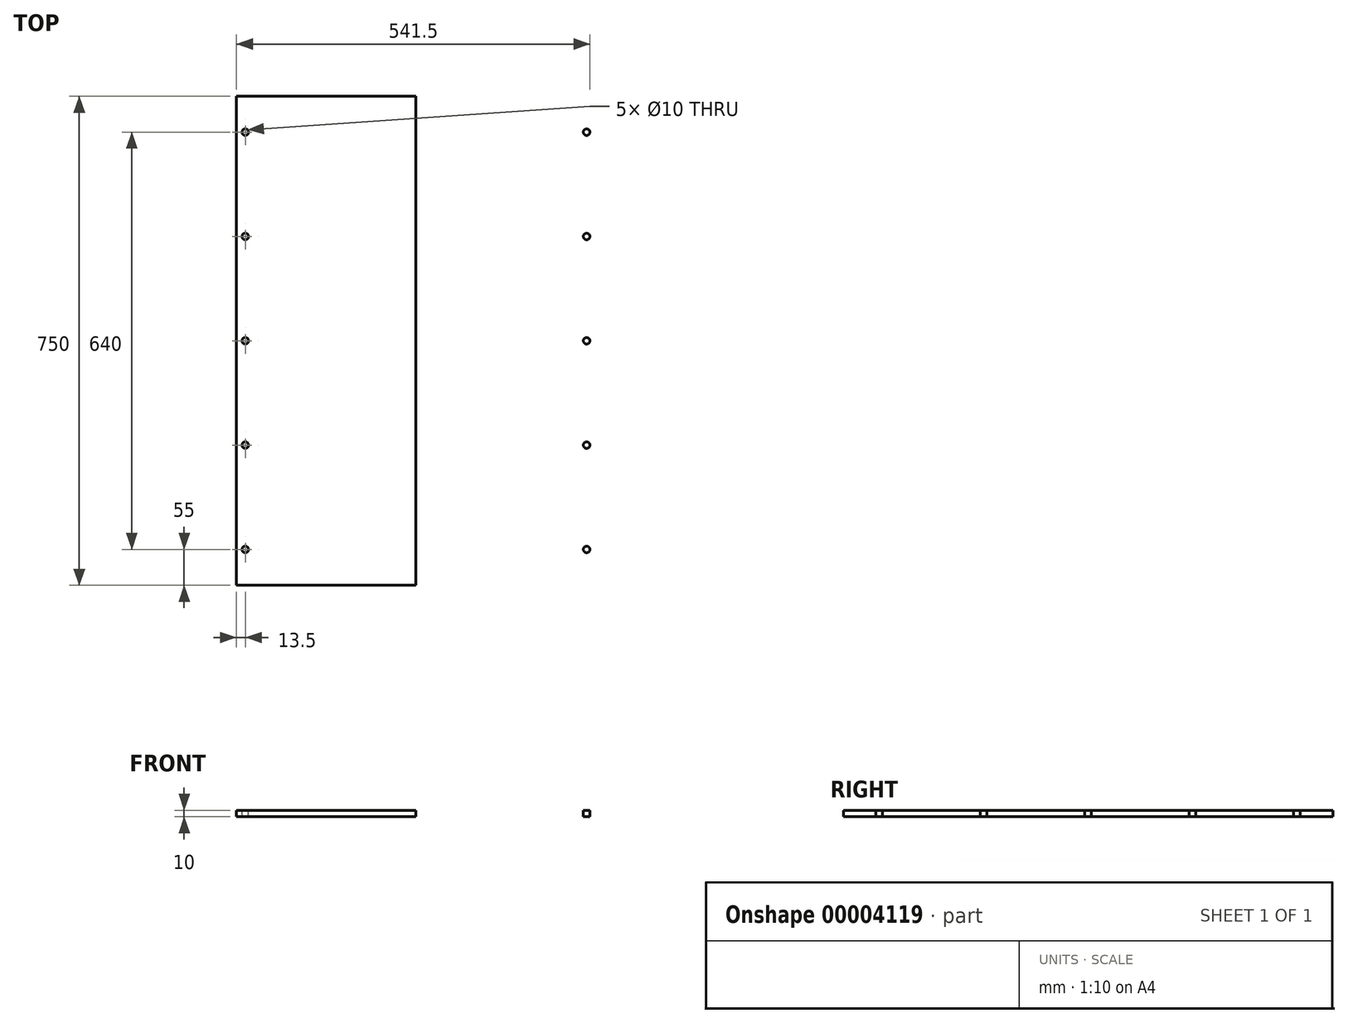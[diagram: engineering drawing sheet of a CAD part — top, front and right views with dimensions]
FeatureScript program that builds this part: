
annotation { "Feature Type Name" : "Feature", "Feature Type Description" : "" }
export const myFeature = defineFeature(function(context is Context, id is Id, definition is map)
    precondition{}
    {
        {
            var Q0;
            Q0=qCreatedBy(makeId("Top.planeOp"),FACE);
            var sketch = newSketch(context, id + "F0", { "sketchPlane" : qUnion([Q0])});
            skLineSegment(sketch, "E0.bottom", {"start": v(0, 0) * mm, "end": v(550, 0) * mm});
            skLineSegment(sketch, "E0.top", {"start": v(0, 750) * mm, "end": v(550, 750) * mm});
            skLineSegment(sketch, "E0.left", {"start": v(0, 0) * mm, "end": v(0, 750) * mm});
            skLineSegment(sketch, "E0.right", {"start": v(550, 0) * mm, "end": v(550, 750) * mm});
            skSolve(sketch);
        }
        {
            var Q0;
            Q0=makeQuery(id+"F0.imprint","IMPRINT",FACE,{"disambiguationData":[TD([[makeQuery(id+"F0.imprint","IMPRINT",EDGE,{"derivedFrom":sQuery(id+"F0.wireOp",EDGE,"E0.bottom")}),1.0]])]});
            extrude(context, id + "F1", {"entities" : qUnion([Q0]), "depth" : 10 * mm});
        }
        {
            var Q0;
            Q0=makeQuery(id+"F1.opExtrude","CAP_FACE",FACE,{"disambiguationData":[OSD([sQuery(id+"F0.wireOp",EDGE,"E0.bottom"),sQuery(id+"F0.wireOp",EDGE,"E0.top"),sQuery(id+"F0.wireOp",EDGE,"E0.left"),sQuery(id+"F0.wireOp",EDGE,"E0.right")])],"isStart":false});
            var sketch = newSketch(context, id + "F2", { "sketchPlane" : qUnion([Q0])});
            skLineSegment(sketch, "E1", {"start": v(13.5, 0) * mm, "end": v(13.5, 750) * mm});
            skCircle(sketch, "E2", {"center": v(13.5, 55) * mm, "radius": 5 * mm});
            skCircle(sketch, "E3.0.1.0", {"center": v(13.5, 215) * mm, "radius": 5 * mm});
            skCircle(sketch, "E3.0.2.0", {"center": v(13.5, 375) * mm, "radius": 5 * mm});
            skCircle(sketch, "E3.0.3.0", {"center": v(13.5, 535) * mm, "radius": 5 * mm});
            skCircle(sketch, "E3.0.4.0", {"center": v(13.5, 695) * mm, "radius": 5 * mm});
            skLineSegment(sketch, "E3.direction1", {"start": v(13.5, 55) * mm, "end": v(52, 55) * mm, "construction": true});
            skLineSegment(sketch, "E3.direction2", {"start": v(13.5, 55) * mm, "end": v(13.5, 215) * mm, "construction": true});
            skLineSegment(sketch, "E4", {"start": v(275, 0) * mm, "end": v(275, 750) * mm});
            skCircle(sketch, "E5.0.MirrorC", {"center": v(536.5, 55) * mm, "radius": 5 * mm});
            skCircle(sketch, "E6.0.MirrorC", {"center": v(536.5, 215) * mm, "radius": 5 * mm});
            skCircle(sketch, "E7.0.MirrorC", {"center": v(536.5, 375) * mm, "radius": 5 * mm});
            skCircle(sketch, "E8.0.MirrorC", {"center": v(536.5, 535) * mm, "radius": 5 * mm});
            skCircle(sketch, "E9.0.MirrorC", {"center": v(536.5, 695) * mm, "radius": 5 * mm});
            skSolve(sketch);
        }
        {
            var Q0;
            {var subQ0=sQuery(id+"F2.wireOp",EDGE,"E2");var subQ1=sQuery(id+"F2.wireOp",EDGE,"E1");var subQ3=makeQuery(id+"F2.imprint","INTERSECT",VERTEX,{"disambiguationData":[OD(0.0)],"derivedFrom":[subQ1,subQ0]});Q0=makeQuery(id+"F2.imprint","IMPRINT",FACE,{"disambiguationData":[TD([[makeQuery(id+"F2.imprint","IMPRINT",EDGE,{"disambiguationData":[TD([[subQ3,-1.0]])],"derivedFrom":subQ1}),1.0]])]});}
            var Q1;
            {var subQ0=sQuery(id+"F2.wireOp",EDGE,"E2");var subQ1=sQuery(id+"F2.wireOp",EDGE,"E1");var subQ3=makeQuery(id+"F2.imprint","INTERSECT",VERTEX,{"disambiguationData":[OD(0.0)],"derivedFrom":[subQ1,subQ0]});Q1=makeQuery(id+"F2.imprint","IMPRINT",FACE,{"disambiguationData":[TD([[makeQuery(id+"F2.imprint","IMPRINT",EDGE,{"disambiguationData":[TD([[subQ3,-1.0]])],"derivedFrom":subQ1}),-1.0]])]});}
            var Q2;
            {var subQ0=sQuery(id+"F2.wireOp",EDGE,"E3.0.1.0");var subQ1=sQuery(id+"F2.wireOp",EDGE,"E1");var subQ3=makeQuery(id+"F2.imprint","INTERSECT",VERTEX,{"disambiguationData":[OD(0.0)],"derivedFrom":[subQ1,subQ0]});Q2=makeQuery(id+"F2.imprint","IMPRINT",FACE,{"disambiguationData":[TD([[makeQuery(id+"F2.imprint","IMPRINT",EDGE,{"disambiguationData":[TD([[subQ3,-1.0]])],"derivedFrom":subQ1}),1.0]])]});}
            var Q3;
            {var subQ0=sQuery(id+"F2.wireOp",EDGE,"E3.0.1.0");var subQ1=sQuery(id+"F2.wireOp",EDGE,"E1");var subQ3=makeQuery(id+"F2.imprint","INTERSECT",VERTEX,{"disambiguationData":[OD(0.0)],"derivedFrom":[subQ1,subQ0]});Q3=makeQuery(id+"F2.imprint","IMPRINT",FACE,{"disambiguationData":[TD([[makeQuery(id+"F2.imprint","IMPRINT",EDGE,{"disambiguationData":[TD([[subQ3,-1.0]])],"derivedFrom":subQ1}),-1.0]])]});}
            var Q4;
            {var subQ0=sQuery(id+"F2.wireOp",EDGE,"E3.0.2.0");var subQ1=sQuery(id+"F2.wireOp",EDGE,"E1");var subQ3=makeQuery(id+"F2.imprint","INTERSECT",VERTEX,{"disambiguationData":[OD(0.0)],"derivedFrom":[subQ1,subQ0]});Q4=makeQuery(id+"F2.imprint","IMPRINT",FACE,{"disambiguationData":[TD([[makeQuery(id+"F2.imprint","IMPRINT",EDGE,{"disambiguationData":[TD([[subQ3,-1.0]])],"derivedFrom":subQ1}),1.0]])]});}
            var Q5;
            {var subQ0=sQuery(id+"F2.wireOp",EDGE,"E3.0.2.0");var subQ1=sQuery(id+"F2.wireOp",EDGE,"E1");var subQ3=makeQuery(id+"F2.imprint","INTERSECT",VERTEX,{"disambiguationData":[OD(0.0)],"derivedFrom":[subQ1,subQ0]});Q5=makeQuery(id+"F2.imprint","IMPRINT",FACE,{"disambiguationData":[TD([[makeQuery(id+"F2.imprint","IMPRINT",EDGE,{"disambiguationData":[TD([[subQ3,-1.0]])],"derivedFrom":subQ1}),-1.0]])]});}
            var Q6;
            {var subQ0=sQuery(id+"F2.wireOp",EDGE,"E3.0.4.0");var subQ1=sQuery(id+"F2.wireOp",EDGE,"E1");var subQ3=makeQuery(id+"F2.imprint","INTERSECT",VERTEX,{"disambiguationData":[OD(0.0)],"derivedFrom":[subQ1,subQ0]});Q6=makeQuery(id+"F2.imprint","IMPRINT",FACE,{"disambiguationData":[TD([[makeQuery(id+"F2.imprint","IMPRINT",EDGE,{"disambiguationData":[TD([[subQ3,-1.0]])],"derivedFrom":subQ1}),1.0]])]});}
            var Q7;
            {var subQ0=sQuery(id+"F2.wireOp",EDGE,"E3.0.4.0");var subQ1=sQuery(id+"F2.wireOp",EDGE,"E1");var subQ3=makeQuery(id+"F2.imprint","INTERSECT",VERTEX,{"disambiguationData":[OD(0.0)],"derivedFrom":[subQ1,subQ0]});Q7=makeQuery(id+"F2.imprint","IMPRINT",FACE,{"disambiguationData":[TD([[makeQuery(id+"F2.imprint","IMPRINT",EDGE,{"disambiguationData":[TD([[subQ3,-1.0]])],"derivedFrom":subQ1}),-1.0]])]});}
            var Q8;
            {var subQ0=sQuery(id+"F2.wireOp",EDGE,"E3.0.3.0");var subQ1=sQuery(id+"F2.wireOp",EDGE,"E1");var subQ3=makeQuery(id+"F2.imprint","INTERSECT",VERTEX,{"disambiguationData":[OD(0.0)],"derivedFrom":[subQ1,subQ0]});Q8=makeQuery(id+"F2.imprint","IMPRINT",FACE,{"disambiguationData":[TD([[makeQuery(id+"F2.imprint","IMPRINT",EDGE,{"disambiguationData":[TD([[subQ3,-1.0]])],"derivedFrom":subQ1}),1.0]])]});}
            var Q9;
            {var subQ0=sQuery(id+"F2.wireOp",EDGE,"E3.0.3.0");var subQ1=sQuery(id+"F2.wireOp",EDGE,"E1");var subQ3=makeQuery(id+"F2.imprint","INTERSECT",VERTEX,{"disambiguationData":[OD(0.0)],"derivedFrom":[subQ1,subQ0]});Q9=makeQuery(id+"F2.imprint","IMPRINT",FACE,{"disambiguationData":[TD([[makeQuery(id+"F2.imprint","IMPRINT",EDGE,{"disambiguationData":[TD([[subQ3,-1.0]])],"derivedFrom":subQ1}),-1.0]])]});}
            var Q10;
            Q10=makeQuery(id+"F2.imprint","IMPRINT",FACE,{"disambiguationData":[TD([[makeQuery(id+"F2.imprint","IMPRINT",EDGE,{"derivedFrom":sQuery(id+"F2.wireOp",EDGE,"E5.0.MirrorC")}),-1.0]])]});
            var Q11;
            Q11=makeQuery(id+"F2.imprint","IMPRINT",FACE,{"disambiguationData":[TD([[makeQuery(id+"F2.imprint","IMPRINT",EDGE,{"derivedFrom":sQuery(id+"F2.wireOp",EDGE,"E6.0.MirrorC")}),-1.0]])]});
            var Q12;
            Q12=makeQuery(id+"F2.imprint","IMPRINT",FACE,{"disambiguationData":[TD([[makeQuery(id+"F2.imprint","IMPRINT",EDGE,{"derivedFrom":sQuery(id+"F2.wireOp",EDGE,"E7.0.MirrorC")}),-1.0]])]});
            var Q13;
            Q13=makeQuery(id+"F2.imprint","IMPRINT",FACE,{"disambiguationData":[TD([[makeQuery(id+"F2.imprint","IMPRINT",EDGE,{"derivedFrom":sQuery(id+"F2.wireOp",EDGE,"E8.0.MirrorC")}),-1.0]])]});
            var Q14;
            Q14=makeQuery(id+"F2.imprint","IMPRINT",FACE,{"disambiguationData":[TD([[makeQuery(id+"F2.imprint","IMPRINT",EDGE,{"derivedFrom":sQuery(id+"F2.wireOp",EDGE,"E9.0.MirrorC")}),-1.0]])]});
            extrude(context, id + "F3", {"entities" : qUnion([Q0, Q1, Q2, Q3, Q4, Q5, Q6, Q7, Q8, Q9, Q10, Q11, Q12, Q13, Q14]), "operationType" : NewBodyOperationType.REMOVE, "oppositeDirection" : true, "depth" : 25 * mm});
        }
    });
